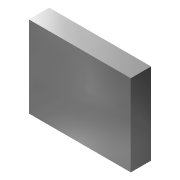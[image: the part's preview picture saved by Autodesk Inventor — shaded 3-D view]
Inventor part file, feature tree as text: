
AUTODESK INVENTOR PART (.ipt)
format: ipt  version: 2015 (Build 190159000, 159)  size: 96,256 bytes
history: native  units: mm
features: extrude x1, sketch x1
ambient origin geometry x8: Origin, YZ Plane, XZ Plane, XY Plane, X Axis, Y Axis, Z Axis, Center Point
bodies: Body1 (feature_tree)
feature tree (2):
  extrude  "Extrusion10"  Depth=40.0mm
  sketch  "Sketch11"  dims[d63=50.0mm d64=40.0mm d65=10.0mm d66=0.0mm]
